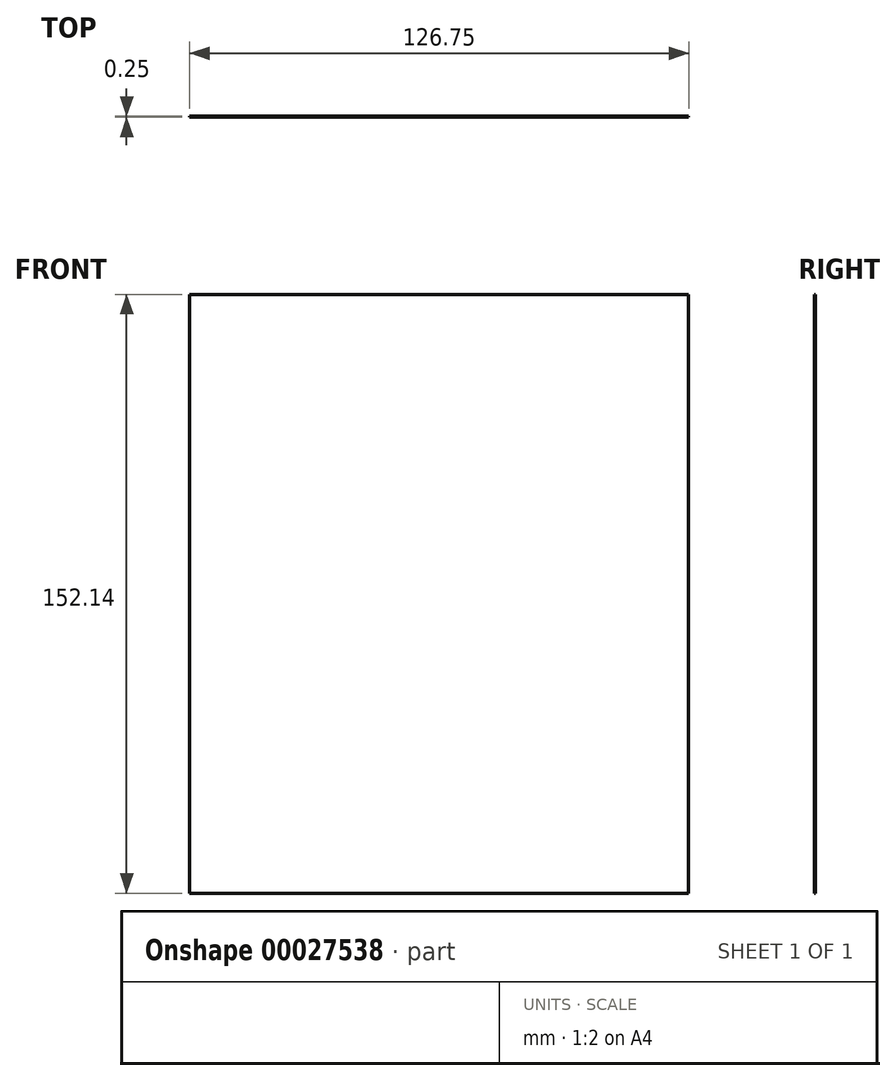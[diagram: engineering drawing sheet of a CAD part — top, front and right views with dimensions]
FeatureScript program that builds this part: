
annotation { "Feature Type Name" : "Feature", "Feature Type Description" : "" }
export const myFeature = defineFeature(function(context is Context, id is Id, definition is map)
    precondition{}
    {
        {
            var Q0;
            Q0=qCreatedBy(makeId("Front.planeOp"),FACE);
            var sketch = newSketch(context, id + "F0", { "sketchPlane" : qUnion([Q0])});
            skLineSegment(sketch, "E0.bottom", {"start": v(-42.7, 126.61) * mm, "end": v(84.04, 126.61) * mm});
            skLineSegment(sketch, "E0.top", {"start": v(-42.7, -25.53) * mm, "end": v(84.04, -25.53) * mm});
            skLineSegment(sketch, "E0.left", {"start": v(-42.7, 126.61) * mm, "end": v(-42.7, -25.53) * mm});
            skLineSegment(sketch, "E0.right", {"start": v(84.04, 126.61) * mm, "end": v(84.04, -25.53) * mm});
            skSolve(sketch);
        }
        {
            var Q0;
            Q0=makeQuery(id+"F0.imprint","IMPRINT",FACE,{"disambiguationData":[TD([[makeQuery(id+"F0.imprint","IMPRINT",EDGE,{"derivedFrom":sQuery(id+"F0.wireOp",EDGE,"E0.bottom")}),-1.0]])]});
            extrude(context, id + "F1", {"entities" : qUnion([Q0]), "depth" : 0.25 * mm});
        }
    });
